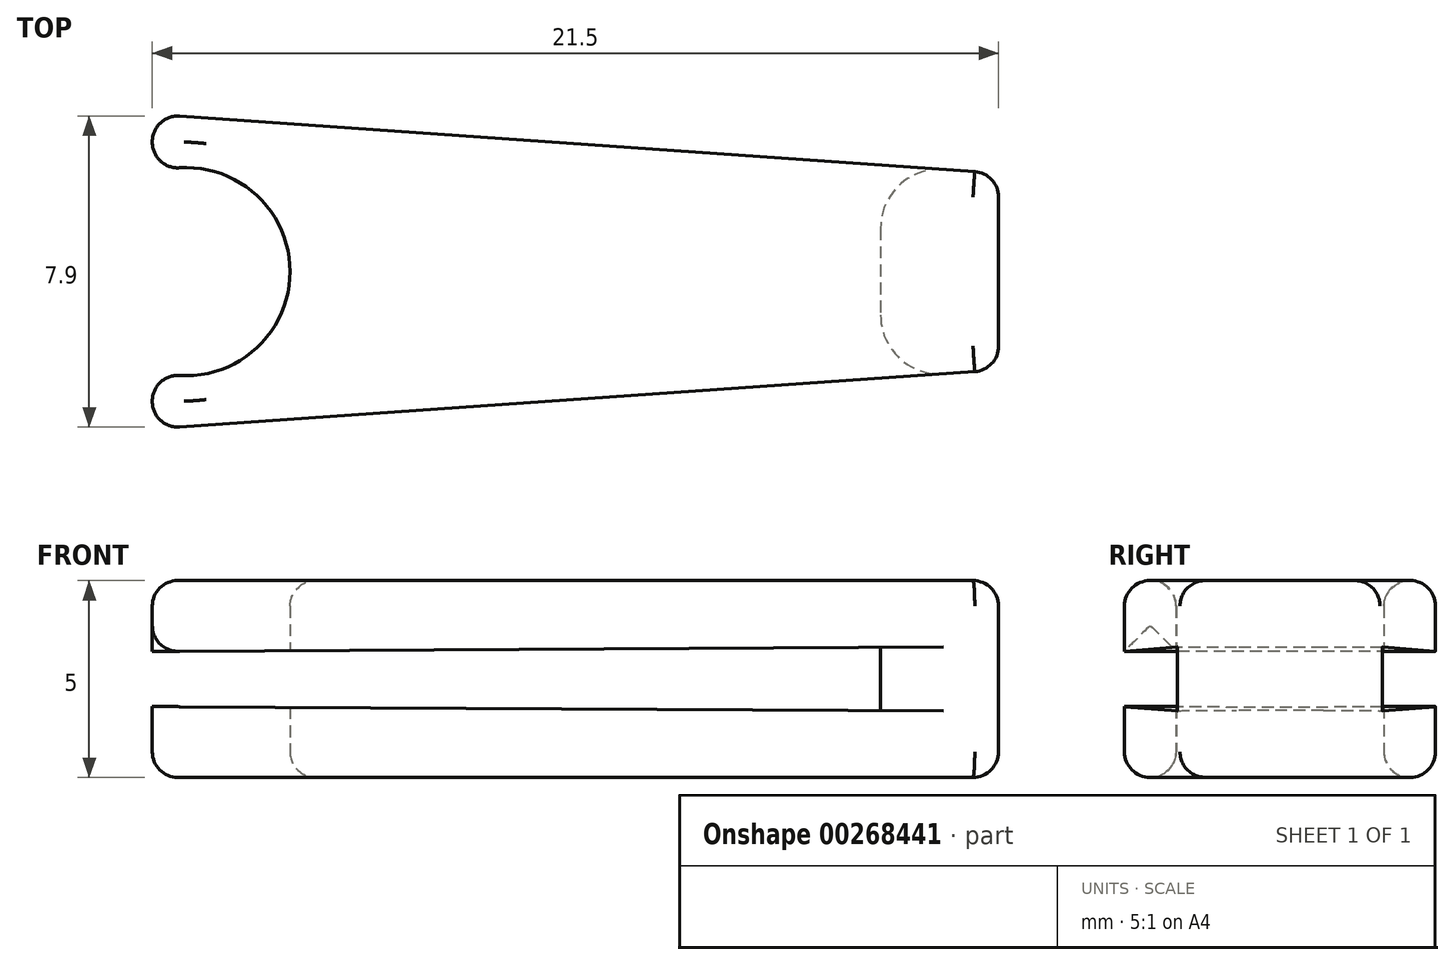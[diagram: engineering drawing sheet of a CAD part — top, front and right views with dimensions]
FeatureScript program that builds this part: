
annotation { "Feature Type Name" : "Feature", "Feature Type Description" : "" }
export const myFeature = defineFeature(function(context is Context, id is Id, definition is map)
    precondition{}
    {
        {
            var Q0;
            Q0=qCreatedBy(makeId("Top.planeOp"),FACE);
            var sketch = newSketch(context, id + "F0", { "sketchPlane" : qUnion([Q0])});
            skLineSegment(sketch, "E0.bottom", {"start": v(10.75, 4) * mm, "end": v(-10.75, 4) * mm});
            skLineSegment(sketch, "E0.top", {"start": v(10.75, -4) * mm, "end": v(-10.75, -4) * mm});
            skLineSegment(sketch, "E0.left", {"start": v(10.75, 4) * mm, "end": v(10.75, -4) * mm});
            skLineSegment(sketch, "E0.right", {"start": v(-10.75, 4) * mm, "end": v(-10.75, -4) * mm});
            skPoint(sketch, "E0.middle", {"position": v(0, 0) * mm});
            skLineSegment(sketch, "E1", {"start": v(10.75, 0) * mm, "end": v(-10.75, 0) * mm, "construction": true});
            skPoint(sketch, "E2", {"position": v(10.75, 2.5) * mm});
            skPoint(sketch, "E3", {"position": v(10.75, -2.5) * mm});
            skLineSegment(sketch, "E4", {"start": v(-10.75, 4) * mm, "end": v(10.75, 2.5) * mm});
            skLineSegment(sketch, "E5", {"start": v(10.75, -2.5) * mm, "end": v(-10.75, -4) * mm});
            skPoint(sketch, "E6", {"position": v(-10.75, 2.5) * mm});
            skPoint(sketch, "E7", {"position": v(-10.75, -2.5) * mm});
            skPoint(sketch, "E8", {"position": v(-7.25, 0) * mm});
            skCircle(sketch, "E9", {"center": v(-9.9, 0) * mm, "radius": 2.64 * mm});
            skSolve(sketch);
        }
        {
            var Q0;
            {var subQ0=sQuery(id+"F0.wireOp",EDGE,"E4");Q0=makeQuery(id+"F0.imprint","IMPRINT",FACE,{"disambiguationData":[TD([[makeQuery(id+"F0.imprint","IMPRINT",EDGE,{"derivedFrom":subQ0}),-1.0]])]});}
            extrude(context, id + "F1", {"entities" : qUnion([Q0]), "depth" : 5 * mm});
        }
        {
            var Q0;
            Q0=qCreatedBy(makeId("Front.planeOp"),FACE);
            var sketch = newSketch(context, id + "F2", { "sketchPlane" : qUnion([Q0])});
            skPoint(sketch, "E10.0", {"position": v(7.75, 0) * mm});
            skPoint(sketch, "E11.0", {"position": v(10.75, 0) * mm});
            skPoint(sketch, "E11.1", {"position": v(10.75, 5) * mm});
            skPoint(sketch, "E11.2", {"position": v(-10.75, 5) * mm});
            skPoint(sketch, "E11.3", {"position": v(-10.75, 0) * mm});
            skLineSegment(sketch, "E12", {"start": v(-10.75, 5) * mm, "end": v(10.75, 5) * mm, "construction": true});
            skLineSegment(sketch, "E13", {"start": v(10.75, 0) * mm, "end": v(7.75, 0) * mm, "construction": true});
            skLineSegment(sketch, "E14", {"start": v(7.75, 0) * mm, "end": v(-10.75, 0) * mm, "construction": true});
            skLineSegment(sketch, "E15", {"start": v(-10.75, 0) * mm, "end": v(-10.75, 5) * mm, "construction": true});
            skLineSegment(sketch, "E16", {"start": v(10.75, 5) * mm, "end": v(10.75, 0) * mm, "construction": true});
            skLineSegment(sketch, "E17", {"start": v(7.75, 0) * mm, "end": v(7.75, 5) * mm, "construction": true});
            skLineSegment(sketch, "E18", {"start": v(-10.75, 2.5) * mm, "end": v(10.75, 2.5) * mm, "construction": true});
            skLineSegment(sketch, "E19", {"start": v(7.75, 3.3) * mm, "end": v(-10.75, 3.2) * mm});
            skLineSegment(sketch, "E20", {"start": v(-10.75, 3.2) * mm, "end": v(-10.75, 1.8) * mm});
            skLineSegment(sketch, "E21", {"start": v(-10.75, 1.8) * mm, "end": v(7.75, 1.7) * mm});
            skLineSegment(sketch, "E22", {"start": v(7.75, 1.7) * mm, "end": v(7.75, 3.3) * mm});
            skPoint(sketch, "E23", {"position": v(7.75, 2.5) * mm});
            skSolve(sketch);
        }
        {
            var Q0;
            Q0=makeQuery(id+"F2.imprint","IMPRINT",FACE,{"disambiguationData":[TD([[makeQuery(id+"F2.imprint","IMPRINT",EDGE,{"derivedFrom":sQuery(id+"F2.wireOp",EDGE,"E19")}),1.0]])]});
            extrude(context, id + "F3", {"entities" : qUnion([Q0]), "operationType" : NewBodyOperationType.REMOVE, "oppositeDirection" : true, "depth" : 25 * mm, "hasSecondDirection" : true, "secondDirectionOppositeDirection" : false, "secondDirectionDepth" : 25 * mm});
        }
        {
            var Q0;
            Q0=makeQuery(id+"F3.boolean.opBoolean","INTERSECT",EDGE,{"derivedFrom":[makeQuery(id+"F1.opExtrude","SWEPT_FACE",FACE,{"disambiguationData":[OSD([sQuery(id+"F0.wireOp",EDGE,"34FWykxQ-RLKL-W02B-jfMP-8d10KNbcjTwG")])]}),makeQuery(id+"F3.opExtrude","SWEPT_FACE",FACE,{"disambiguationData":[OSD([sQuery(id+"F2.wireOp",EDGE,"E19")])]})]});
            var Q1;
            Q1=makeQuery(id+"F3.boolean.opBoolean","INTERSECT",EDGE,{"derivedFrom":[makeQuery(id+"F1.opExtrude","SWEPT_FACE",FACE,{"disambiguationData":[OSD([sQuery(id+"F0.wireOp",EDGE,"34FWykxQ-RLKL-W02B-jfMP-8d10KNbcjTwG")])]}),makeQuery(id+"F3.opExtrude","SWEPT_FACE",FACE,{"disambiguationData":[OSD([sQuery(id+"F2.wireOp",EDGE,"E21")])]})]});
            var Q2;
            Q2=makeQuery(id+"F1.opExtrude","CAP_FACE",FACE,{"disambiguationData":[OSD([sQuery(id+"F0.wireOp",EDGE,"E0.left"),sQuery(id+"F0.wireOp",EDGE,"E0.right"),sQuery(id+"F0.wireOp",EDGE,"E4"),sQuery(id+"F0.wireOp",EDGE,"E5"),sQuery(id+"F0.wireOp",EDGE,"34FWykxQ-RLKL-W02B-jfMP-8d10KNbcjTwG")])],"isStart":false});
            var Q3;
            Q3=makeQuery(id+"F1.opExtrude","CAP_FACE",FACE,{"disambiguationData":[OSD([sQuery(id+"F0.wireOp",EDGE,"E0.left"),sQuery(id+"F0.wireOp",EDGE,"E0.right"),sQuery(id+"F0.wireOp",EDGE,"E4"),sQuery(id+"F0.wireOp",EDGE,"E5"),sQuery(id+"F0.wireOp",EDGE,"34FWykxQ-RLKL-W02B-jfMP-8d10KNbcjTwG")])],"isStart":true});
            var Q4;
            {var subQ1=sQuery(id+"F0.wireOp",EDGE,"E5");var subQ2=sQuery(id+"F0.wireOp",EDGE,"E0.right");var subQ3=sQuery(id+"F0.wireOp",EDGE,"E0.top");Q4=makeQuery(id+"F3.boolean.opBoolean","SPLIT",EDGE,{"disambiguationData":[TD([makeQuery(id+"F3.opExtrude","SWEPT_FACE",FACE,{"disambiguationData":[OSD([sQuery(id+"F2.wireOp",EDGE,"E19")])]})])],"derivedFrom":makeQuery(id+"F1.opExtrude","SWEPT_EDGE",EDGE,{"disambiguationData":[OSD([subQ3,subQ2,subQ1])]})});}
            var Q5;
            {var subQ1=sQuery(id+"F0.wireOp",EDGE,"E5");var subQ2=sQuery(id+"F0.wireOp",EDGE,"E0.right");var subQ3=sQuery(id+"F0.wireOp",EDGE,"E0.top");Q5=makeQuery(id+"F3.boolean.opBoolean","SPLIT",EDGE,{"disambiguationData":[TD([makeQuery(id+"F3.opExtrude","SWEPT_FACE",FACE,{"disambiguationData":[OSD([sQuery(id+"F2.wireOp",EDGE,"E21")])]})])],"derivedFrom":makeQuery(id+"F1.opExtrude","SWEPT_EDGE",EDGE,{"disambiguationData":[OSD([subQ3,subQ2,subQ1])]})});}
            var Q6;
            {var subQ1=sQuery(id+"F0.wireOp",EDGE,"E4");var subQ2=sQuery(id+"F0.wireOp",EDGE,"E0.right");var subQ3=sQuery(id+"F0.wireOp",EDGE,"E0.bottom");Q6=makeQuery(id+"F3.boolean.opBoolean","SPLIT",EDGE,{"disambiguationData":[TD([makeQuery(id+"F3.opExtrude","SWEPT_FACE",FACE,{"disambiguationData":[OSD([sQuery(id+"F2.wireOp",EDGE,"E21")])]})])],"derivedFrom":makeQuery(id+"F1.opExtrude","SWEPT_EDGE",EDGE,{"disambiguationData":[OSD([subQ3,subQ2,subQ1])]})});}
            var Q7;
            {var subQ1=sQuery(id+"F0.wireOp",EDGE,"E4");var subQ2=sQuery(id+"F0.wireOp",EDGE,"E0.right");var subQ3=sQuery(id+"F0.wireOp",EDGE,"E0.bottom");Q7=makeQuery(id+"F3.boolean.opBoolean","SPLIT",EDGE,{"disambiguationData":[TD([makeQuery(id+"F3.opExtrude","SWEPT_FACE",FACE,{"disambiguationData":[OSD([sQuery(id+"F2.wireOp",EDGE,"E19")])]})])],"derivedFrom":makeQuery(id+"F1.opExtrude","SWEPT_EDGE",EDGE,{"disambiguationData":[OSD([subQ3,subQ2,subQ1])]})});}
            var Q8;
            {var subQ0=sQuery(id+"F0.wireOp",EDGE,"E9");var subQ2=sQuery(id+"F0.wireOp",EDGE,"E0.right");var subQ3=makeQuery(id+"F0.imprint","INTERSECT",VERTEX,{"disambiguationData":[OD(1.0)],"derivedFrom":[subQ2,subQ0]});Q8=makeQuery(id+"F3.boolean.opBoolean","SPLIT",EDGE,{"disambiguationData":[TD([makeQuery(id+"F3.opExtrude","SWEPT_FACE",FACE,{"disambiguationData":[OSD([sQuery(id+"F2.wireOp",EDGE,"E19")])]})])],"derivedFrom":makeQuery(id+"F1.opExtrude","SWEPT_EDGE",EDGE,{"disambiguationData":[OSD([subQ2,subQ0]),TDD([subQ3])]})});}
            var Q9;
            {var subQ0=sQuery(id+"F0.wireOp",EDGE,"E9");var subQ2=sQuery(id+"F0.wireOp",EDGE,"E0.right");var subQ3=makeQuery(id+"F0.imprint","INTERSECT",VERTEX,{"disambiguationData":[OD(1.0)],"derivedFrom":[subQ2,subQ0]});Q9=makeQuery(id+"F3.boolean.opBoolean","SPLIT",EDGE,{"disambiguationData":[TD([makeQuery(id+"F3.opExtrude","SWEPT_FACE",FACE,{"disambiguationData":[OSD([sQuery(id+"F2.wireOp",EDGE,"E21")])]})])],"derivedFrom":makeQuery(id+"F1.opExtrude","SWEPT_EDGE",EDGE,{"disambiguationData":[OSD([subQ2,subQ0]),TDD([subQ3])]})});}
            var Q10;
            {var subQ0=sQuery(id+"F0.wireOp",EDGE,"E9");var subQ2=sQuery(id+"F0.wireOp",EDGE,"E0.right");var subQ3=makeQuery(id+"F0.imprint","INTERSECT",VERTEX,{"disambiguationData":[OD(0.0)],"derivedFrom":[subQ2,subQ0]});Q10=makeQuery(id+"F3.boolean.opBoolean","SPLIT",EDGE,{"disambiguationData":[TD([makeQuery(id+"F3.opExtrude","SWEPT_FACE",FACE,{"disambiguationData":[OSD([sQuery(id+"F2.wireOp",EDGE,"E19")])]})])],"derivedFrom":makeQuery(id+"F1.opExtrude","SWEPT_EDGE",EDGE,{"disambiguationData":[OSD([subQ2,subQ0]),TDD([subQ3])]})});}
            var Q11;
            {var subQ0=sQuery(id+"F0.wireOp",EDGE,"E9");var subQ2=sQuery(id+"F0.wireOp",EDGE,"E0.right");var subQ3=makeQuery(id+"F0.imprint","INTERSECT",VERTEX,{"disambiguationData":[OD(0.0)],"derivedFrom":[subQ2,subQ0]});Q11=makeQuery(id+"F3.boolean.opBoolean","SPLIT",EDGE,{"disambiguationData":[TD([makeQuery(id+"F3.opExtrude","SWEPT_FACE",FACE,{"disambiguationData":[OSD([sQuery(id+"F2.wireOp",EDGE,"E21")])]})])],"derivedFrom":makeQuery(id+"F1.opExtrude","SWEPT_EDGE",EDGE,{"disambiguationData":[OSD([subQ2,subQ0]),TDD([subQ3])]})});}
            var Q12;
            Q12=makeQuery(id+"F1.opExtrude","SWEPT_EDGE",EDGE,{"disambiguationData":[OSD([sQuery(id+"F0.wireOp",EDGE,"E0.left"),sQuery(id+"F0.wireOp",EDGE,"E4")])]});
            var Q13;
            Q13=makeQuery(id+"F1.opExtrude","SWEPT_FACE",FACE,{"disambiguationData":[OSD([sQuery(id+"F0.wireOp",EDGE,"E0.left")])]});
            var Q14;
            {var subQ0=sQuery(id+"F0.wireOp",EDGE,"E9");var subQ2=sQuery(id+"F0.wireOp",EDGE,"E0.right");Q14=makeQuery(id+"F3.boolean.opBoolean","SPLIT",FACE,{"disambiguationData":[TD([makeQuery(id+"F3.opExtrude","SWEPT_FACE",FACE,{"disambiguationData":[OSD([sQuery(id+"F2.wireOp",EDGE,"E19")])]})])],"derivedFrom":makeQuery(id+"F1.opExtrude","SWEPT_FACE",FACE,{"disambiguationData":[OSD([subQ2]),TDD([makeQuery(id+"F0.imprint","IMPRINT",EDGE,{"disambiguationData":[TD([[makeQuery(id+"F0.imprint","INTERSECT",VERTEX,{"disambiguationData":[OD(1.0)],"derivedFrom":[subQ2,subQ0]}),-1.0]])],"derivedFrom":subQ2})])]})});}
            var Q15;
            {var subQ0=sQuery(id+"F0.wireOp",EDGE,"E4");var subQ3=sQuery(id+"F2.wireOp",EDGE,"E19");Q15=makeQuery(id+"F3.boolean.opBoolean","COPY",EDGE,{"disambiguationData":[TD([makeQuery(id+"F1.opExtrude","SWEPT_FACE",FACE,{"disambiguationData":[OSD([subQ0])]})])],"derivedFrom":makeQuery(id+"F3.opExtrude","SWEPT_EDGE",EDGE,{"disambiguationData":[OSD([subQ3,sQuery(id+"F2.wireOp",EDGE,"E20")])]})});}
            var Q16;
            {var subQ0=sQuery(id+"F0.wireOp",EDGE,"E5");var subQ3=sQuery(id+"F2.wireOp",EDGE,"E21");Q16=makeQuery(id+"F3.boolean.opBoolean","COPY",EDGE,{"disambiguationData":[TD([makeQuery(id+"F1.opExtrude","SWEPT_FACE",FACE,{"disambiguationData":[OSD([subQ0])]})])],"derivedFrom":makeQuery(id+"F3.opExtrude","SWEPT_EDGE",EDGE,{"disambiguationData":[OSD([sQuery(id+"F2.wireOp",EDGE,"E20"),subQ3])]})});}
            var Q17;
            {var subQ0=sQuery(id+"F0.wireOp",EDGE,"E4");var subQ3=sQuery(id+"F2.wireOp",EDGE,"E21");Q17=makeQuery(id+"F3.boolean.opBoolean","COPY",EDGE,{"disambiguationData":[TD([makeQuery(id+"F1.opExtrude","SWEPT_FACE",FACE,{"disambiguationData":[OSD([subQ0])]})])],"derivedFrom":makeQuery(id+"F3.opExtrude","SWEPT_EDGE",EDGE,{"disambiguationData":[OSD([sQuery(id+"F2.wireOp",EDGE,"E20"),subQ3])]})});}
            fillet(context, id + "F4", {"entities" : qUnion([Q0, Q1, Q2, Q3, Q4, Q5, Q6, Q7, Q8, Q9, Q10, Q11, Q12, Q13, Q14, Q15, Q16, Q17]), "radius" : .65 * mm, "tangentPropagation" : true, "allowEdgeOverflow" : false});
        }
        {
            var Q0;
            Q0=makeQuery(id+"F3.boolean.opBoolean","INTERSECT",EDGE,{"derivedFrom":[makeQuery(id+"F1.opExtrude","SWEPT_FACE",FACE,{"disambiguationData":[OSD([sQuery(id+"F0.wireOp",EDGE,"E4")])]}),makeQuery(id+"F3.opExtrude","SWEPT_FACE",FACE,{"disambiguationData":[OSD([sQuery(id+"F2.wireOp",EDGE,"E22")])]})]});
            var Q1;
            Q1=makeQuery(id+"F3.boolean.opBoolean","INTERSECT",EDGE,{"derivedFrom":[makeQuery(id+"F1.opExtrude","SWEPT_FACE",FACE,{"disambiguationData":[OSD([sQuery(id+"F0.wireOp",EDGE,"E5")])]}),makeQuery(id+"F3.opExtrude","SWEPT_FACE",FACE,{"disambiguationData":[OSD([sQuery(id+"F2.wireOp",EDGE,"E22")])]})]});
            fillet(context, id + "F5", {"entities" : qUnion([Q0, Q1]), "radius" : 1.5 * mm, "tangentPropagation" : true, "allowEdgeOverflow" : false});
        }
    });
